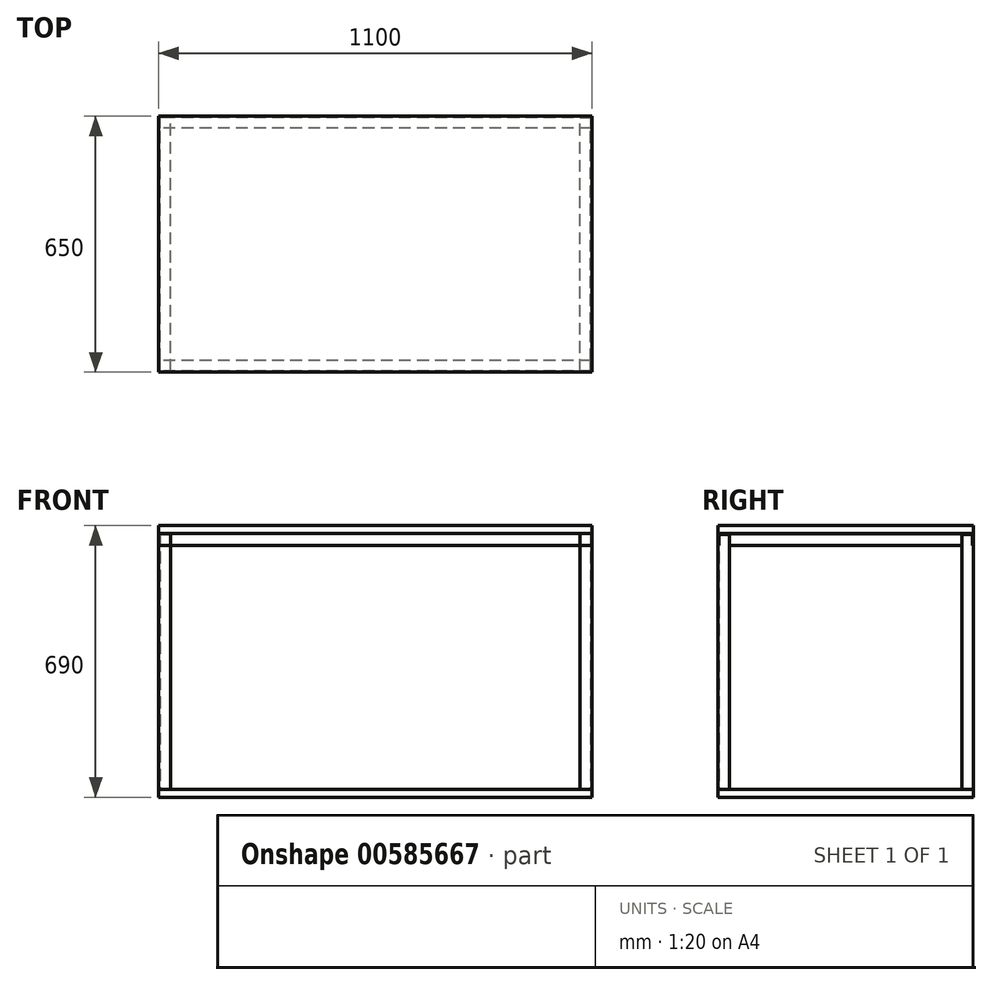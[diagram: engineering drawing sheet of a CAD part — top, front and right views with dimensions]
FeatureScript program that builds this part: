
annotation { "Feature Type Name" : "Feature", "Feature Type Description" : "" }
export const myFeature = defineFeature(function(context is Context, id is Id, definition is map)
    precondition{}
    {
        {
            var Q0;
            Q0=qCreatedBy(makeId("Top.planeOp"),FACE);
            var sketch = newSketch(context, id + "F0", { "sketchPlane" : qUnion([Q0])});
            skLineSegment(sketch, "E0.bottom", {"start": v(-550, 325) * mm, "end": v(550, 325) * mm});
            skLineSegment(sketch, "E0.top", {"start": v(-550, -325) * mm, "end": v(550, -325) * mm});
            skLineSegment(sketch, "E0.left", {"start": v(-550, 325) * mm, "end": v(-550, -325) * mm});
            skLineSegment(sketch, "E0.right", {"start": v(550, 325) * mm, "end": v(550, -325) * mm});
            skPoint(sketch, "E1", {"position": v(0, 325) * mm});
            skPoint(sketch, "E2", {"position": v(-550, 0) * mm});
            skSolve(sketch);
        }
        {
            var Q0;
            Q0=makeQuery(id+"F0.imprint","IMPRINT",FACE,{"disambiguationData":[TD([[makeQuery(id+"F0.imprint","IMPRINT",EDGE,{"derivedFrom":sQuery(id+"F0.wireOp",EDGE,"E0.bottom")}),-1.0]])]});
            extrude(context, id + "F1", {"entities" : qUnion([Q0]), "oppositeDirection" : true, "depth" : 20 * mm, "offsetDistance" : 25 * mm});
        }
        {
            var Q0;
            Q0=qCreatedBy(makeId("Top.planeOp"),FACE);
            cPlane(context, id + "F2", {"entities" : qUnion([Q0]), "cplaneType" : CPlaneType.OFFSET, "offset" : 650 * mm, "width" : 150 * mm, "height" : 150 * mm});
        }
        {
            var Q0;
            Q0=qCreatedBy(id+"F2.planeOp",FACE);
            var sketch = newSketch(context, id + "F3", { "sketchPlane" : qUnion([Q0])});
            skLineSegment(sketch, "E3.bottom", {"start": v(-550, 325) * mm, "end": v(550, 325) * mm});
            skLineSegment(sketch, "E3.top", {"start": v(-550, -325) * mm, "end": v(550, -325) * mm});
            skLineSegment(sketch, "E3.left", {"start": v(-550, 325) * mm, "end": v(-550, -325) * mm});
            skLineSegment(sketch, "E3.right", {"start": v(550, 325) * mm, "end": v(550, -325) * mm});
            skSolve(sketch);
        }
        {
            var Q0;
            Q0 = qSketchRegion(id + "F3", true);
            extrude(context, id + "F4", {"entities" : qUnion([Q0]), "depth" : 20 * mm, "offsetDistance" : 25 * mm});
        }
        {
            var Q0;
            Q0=makeQuery(id+"F1.opExtrude","CAP_FACE",FACE,{"disambiguationData":[OSD([sQuery(id+"F0.wireOp",EDGE,"E0.bottom"),sQuery(id+"F0.wireOp",EDGE,"E0.top"),sQuery(id+"F0.wireOp",EDGE,"E0.left"),sQuery(id+"F0.wireOp",EDGE,"E0.right")])],"isStart":true});
            var sketch = newSketch(context, id + "F5", { "sketchPlane" : qUnion([Q0])});
            skLineSegment(sketch, "E4", {"start": v(-550, -295) * mm, "end": v(-550, -325) * mm});
            skLineSegment(sketch, "E5", {"start": v(-550, -325) * mm, "end": v(-520, -325) * mm});
            skLineSegment(sketch, "E6", {"start": v(-520, -325) * mm, "end": v(-520, -322) * mm});
            skLineSegment(sketch, "E7", {"start": v(-520, -322) * mm, "end": v(-547, -322) * mm});
            skLineSegment(sketch, "E8", {"start": v(-547, -322) * mm, "end": v(-547, -295) * mm});
            skLineSegment(sketch, "E9", {"start": v(-547, -295) * mm, "end": v(-550, -295) * mm});
            skSolve(sketch);
        }
        {
            var Q0;
            Q0 = qSketchRegion(id + "F5", true);
            extrude(context, id + "F6", {"entities" : qUnion([Q0]), "endBound" : BoundingType.UP_TO_NEXT, "depth" : 25 * mm, "offsetDistance" : 25 * mm});
        }
        {
            var Q0;
            Q0=makeQuery(id+"F6.opExtrude","SWEPT_BODY",BODY,{"disambiguationData":[OSD([sQuery(id+"F5.wireOp",EDGE,"E4"),sQuery(id+"F5.wireOp",EDGE,"E5"),sQuery(id+"F5.wireOp",EDGE,"E6"),sQuery(id+"F5.wireOp",EDGE,"E7"),sQuery(id+"F5.wireOp",EDGE,"E8"),sQuery(id+"F5.wireOp",EDGE,"E9")])]});
            var Q1;
            Q1=qCreatedBy(makeId("Front.planeOp"),FACE);
            mirror(context, id + "F7", {"entities" : qUnion([Q0]), "mirrorPlane" : qUnion([Q1])});
        }
        {
            var Q0;
            Q0=makeQuery(id+"F7.opPattern","COPY",BODY,{"derivedFrom":makeQuery(id+"F6.opExtrude","SWEPT_BODY",BODY,{"disambiguationData":[OSD([sQuery(id+"F5.wireOp",EDGE,"E4"),sQuery(id+"F5.wireOp",EDGE,"E5"),sQuery(id+"F5.wireOp",EDGE,"E6"),sQuery(id+"F5.wireOp",EDGE,"E7"),sQuery(id+"F5.wireOp",EDGE,"E8"),sQuery(id+"F5.wireOp",EDGE,"E9")])]}),"instanceName":"1"});
            var Q1;
            Q1=makeQuery(id+"F6.opExtrude","SWEPT_BODY",BODY,{"disambiguationData":[OSD([sQuery(id+"F5.wireOp",EDGE,"E4"),sQuery(id+"F5.wireOp",EDGE,"E5"),sQuery(id+"F5.wireOp",EDGE,"E6"),sQuery(id+"F5.wireOp",EDGE,"E7"),sQuery(id+"F5.wireOp",EDGE,"E8"),sQuery(id+"F5.wireOp",EDGE,"E9")])]});
            var Q2;
            Q2=qCreatedBy(makeId("Right.planeOp"),FACE);
            mirror(context, id + "F8", {"entities" : qUnion([Q0, Q1]), "mirrorPlane" : qUnion([Q2])});
        }
        {
            var Q0;
            Q0=qCreatedBy(makeId("Front.planeOp"),FACE);
            var sketch = newSketch(context, id + "F9", { "sketchPlane" : qUnion([Q0])});
            skLineSegment(sketch, "E10", {"start": v(-520, 650) * mm, "end": v(-550, 650) * mm});
            skLineSegment(sketch, "E11", {"start": v(-550, 650) * mm, "end": v(-550, 620) * mm});
            skLineSegment(sketch, "E12", {"start": v(-550, 620) * mm, "end": v(-547, 620) * mm});
            skLineSegment(sketch, "E13", {"start": v(-547, 620) * mm, "end": v(-547, 647) * mm});
            skLineSegment(sketch, "E14", {"start": v(-547, 647) * mm, "end": v(-520, 647) * mm});
            skLineSegment(sketch, "E15", {"start": v(-520, 647) * mm, "end": v(-520, 650) * mm});
            skSolve(sketch);
        }
        {
            var Q0;
            Q0=makeQuery(id+"F9.imprint","IMPRINT",FACE,{"disambiguationData":[TD([[makeQuery(id+"F9.imprint","IMPRINT",EDGE,{"derivedFrom":sQuery(id+"F9.wireOp",EDGE,"E10")}),1.0]])]});
            extrude(context, id + "F10", {"entities" : qUnion([Q0]), "endBound" : BoundingType.UP_TO_NEXT, "depth" : 25 * mm, "offsetDistance" : 25 * mm, "hasSecondDirection" : true, "secondDirectionBound" : SecondDirectionBoundingType.UP_TO_NEXT, "secondDirectionOppositeDirection" : true, "secondDirectionDepth" : 25 * mm});
        }
        {
            var Q0;
            Q0=makeQuery(id+"F10.opExtrude","SWEPT_BODY",BODY,{"disambiguationData":[OSD([sQuery(id+"F9.wireOp",EDGE,"E10"),sQuery(id+"F9.wireOp",EDGE,"E11"),sQuery(id+"F9.wireOp",EDGE,"E12"),sQuery(id+"F9.wireOp",EDGE,"E13"),sQuery(id+"F9.wireOp",EDGE,"E14"),sQuery(id+"F9.wireOp",EDGE,"E15")])]});
            var Q1;
            Q1=qCreatedBy(makeId("Right.planeOp"),FACE);
            mirror(context, id + "F11", {"entities" : qUnion([Q0]), "mirrorPlane" : qUnion([Q1])});
        }
        {
            var Q0;
            Q0=qCreatedBy(makeId("Right.planeOp"),FACE);
            var sketch = newSketch(context, id + "F12", { "sketchPlane" : qUnion([Q0])});
            skLineSegment(sketch, "E16", {"start": v(-325, 650) * mm, "end": v(-325, 620) * mm});
            skLineSegment(sketch, "E17", {"start": v(-325, 620) * mm, "end": v(-322, 620) * mm});
            skLineSegment(sketch, "E18", {"start": v(-322, 620) * mm, "end": v(-322, 647) * mm});
            skLineSegment(sketch, "E19", {"start": v(-322, 647) * mm, "end": v(-295, 647) * mm});
            skLineSegment(sketch, "E20", {"start": v(-295, 647) * mm, "end": v(-295, 650) * mm});
            skLineSegment(sketch, "E21", {"start": v(-295, 650) * mm, "end": v(-325, 650) * mm});
            skSolve(sketch);
        }
        {
            var Q0;
            Q0=makeQuery(id+"F12.imprint","IMPRINT",FACE,{"disambiguationData":[TD([[makeQuery(id+"F12.imprint","IMPRINT",EDGE,{"derivedFrom":sQuery(id+"F12.wireOp",EDGE,"E16")}),1.0]])]});
            var Q1;
            Q1=makeQuery(id+"F4.opExtrude","SWEPT_FACE",FACE,{"disambiguationData":[OSD([sQuery(id+"F3.wireOp",EDGE,"E3.right")])]});
            var Q2;
            Q2=makeQuery(id+"F4.opExtrude","SWEPT_FACE",FACE,{"disambiguationData":[OSD([sQuery(id+"F3.wireOp",EDGE,"E3.left")])]});
            extrude(context, id + "F13", {"entities" : qUnion([Q0]), "endBound" : BoundingType.UP_TO_SURFACE, "depth" : 25 * mm, "endBoundEntityFace" : qUnion([Q1]), "offsetDistance" : 25 * mm, "hasSecondDirection" : true, "secondDirectionBound" : SecondDirectionBoundingType.UP_TO_SURFACE, "secondDirectionOppositeDirection" : true, "secondDirectionDepth" : 25 * mm, "secondDirectionBoundEntityFace" : qUnion([Q2])});
        }
        {
            var Q0;
            Q0=makeQuery(id+"F13.opExtrude","SWEPT_BODY",BODY,{"disambiguationData":[OSD([sQuery(id+"F12.wireOp",EDGE,"E16"),sQuery(id+"F12.wireOp",EDGE,"E17"),sQuery(id+"F12.wireOp",EDGE,"E18"),sQuery(id+"F12.wireOp",EDGE,"E19"),sQuery(id+"F12.wireOp",EDGE,"E20"),sQuery(id+"F12.wireOp",EDGE,"E21")])]});
            var Q1;
            Q1=qCreatedBy(makeId("Front.planeOp"),FACE);
            mirror(context, id + "F14", {"entities" : qUnion([Q0]), "mirrorPlane" : qUnion([Q1])});
        }
    });
